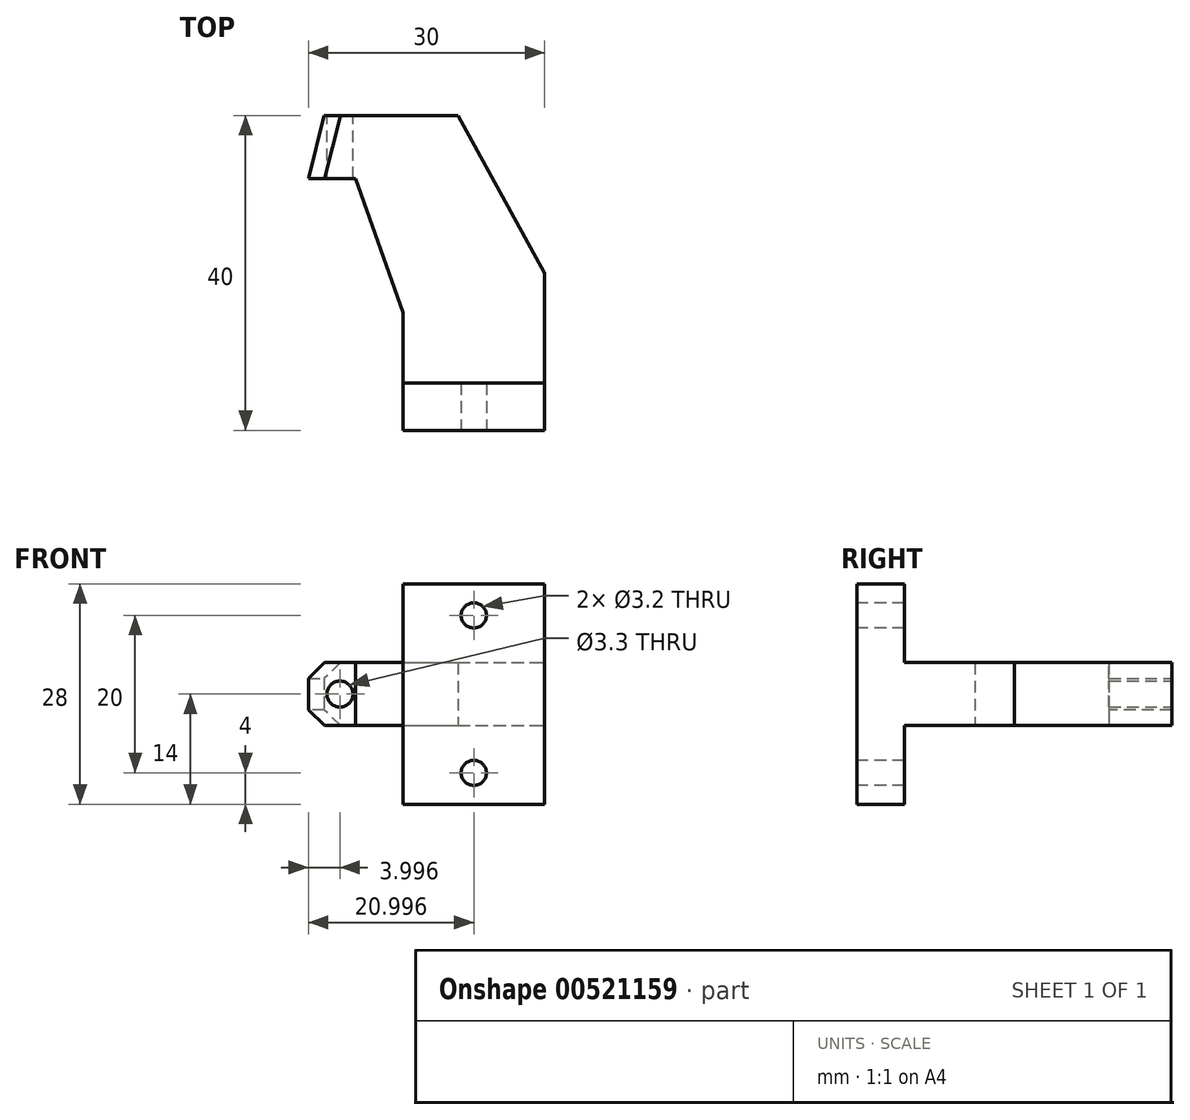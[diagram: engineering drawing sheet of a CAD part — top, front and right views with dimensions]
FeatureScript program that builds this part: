
annotation { "Feature Type Name" : "Feature", "Feature Type Description" : "" }
export const myFeature = defineFeature(function(context is Context, id is Id, definition is map)
    precondition{}
    {
        {
            var Q0;
            Q0=qCreatedBy(makeId("Top.planeOp"),FACE);
            var sketch = newSketch(context, id + "F0", { "sketchPlane" : qUnion([Q0])});
            skLineSegment(sketch, "E0", {"start": v(-19.88, 17) * mm, "end": v(-17.88, 25) * mm});
            skLineSegment(sketch, "E1", {"start": v(-17.88, 25) * mm, "end": v(-0.88, 25) * mm});
            skLineSegment(sketch, "E2", {"start": v(-0.88, 25) * mm, "end": v(10.12, 5) * mm});
            skLineSegment(sketch, "E3", {"start": v(10.12, 5) * mm, "end": v(10.12, -15) * mm});
            skLineSegment(sketch, "E4", {"start": v(-7.88, -15) * mm, "end": v(-7.88, 0) * mm});
            skLineSegment(sketch, "E5", {"start": v(-7.88, 0) * mm, "end": v(-13.88, 17) * mm});
            skLineSegment(sketch, "E6", {"start": v(-13.88, 17) * mm, "end": v(-19.88, 17) * mm});
            skLineSegment(sketch, "E7", {"start": v(-7.88, -15) * mm, "end": v(10.12, -15) * mm});
            skSolve(sketch);
        }
        {
            var Q0;
            Q0 = qSketchRegion(id + "F0", true);
            extrude(context, id + "F1", {"entities" : qUnion([Q0]), "depth" : 8 * mm, "offsetDistance" : 25 * mm});
        }
        {
            var Q0;
            Q0=makeQuery(id+"F1.opExtrude","CAP_FACE",FACE,{"disambiguationData":[OSD([sQuery(id+"F0.wireOp",EDGE,"E0"),sQuery(id+"F0.wireOp",EDGE,"E1"),sQuery(id+"F0.wireOp",EDGE,"E2"),sQuery(id+"F0.wireOp",EDGE,"E3"),sQuery(id+"F0.wireOp",EDGE,"E4"),sQuery(id+"F0.wireOp",EDGE,"E5"),sQuery(id+"F0.wireOp",EDGE,"E6"),sQuery(id+"F0.wireOp",EDGE,"E7")])],"isStart":false});
            var sketch = newSketch(context, id + "F2", { "sketchPlane" : qUnion([Q0])});
            skLineSegment(sketch, "E8.bottom", {"start": v(-7.88, -15) * mm, "end": v(10.12, -15) * mm});
            skLineSegment(sketch, "E8.top", {"start": v(-7.88, -9) * mm, "end": v(10.12, -9) * mm});
            skLineSegment(sketch, "E8.left", {"start": v(-7.88, -15) * mm, "end": v(-7.88, -9) * mm});
            skLineSegment(sketch, "E8.right", {"start": v(10.12, -15) * mm, "end": v(10.12, -9) * mm});
            skSolve(sketch);
        }
        {
            var Q0;
            Q0 = qSketchRegion(id + "F2", true);
            extrude(context, id + "F3", {"entities" : qUnion([Q0]), "operationType" : NewBodyOperationType.ADD, "depth" : 10 * mm, "offsetDistance" : 25 * mm});
        }
        {
            var Q0;
            Q0=makeQuery(id+"F1.opExtrude","CAP_FACE",FACE,{"disambiguationData":[OSD([sQuery(id+"F0.wireOp",EDGE,"E0"),sQuery(id+"F0.wireOp",EDGE,"E1"),sQuery(id+"F0.wireOp",EDGE,"E2"),sQuery(id+"F0.wireOp",EDGE,"E3"),sQuery(id+"F0.wireOp",EDGE,"E4"),sQuery(id+"F0.wireOp",EDGE,"E5"),sQuery(id+"F0.wireOp",EDGE,"E6"),sQuery(id+"F0.wireOp",EDGE,"E7")])],"isStart":true});
            var sketch = newSketch(context, id + "F4", { "sketchPlane" : qUnion([Q0])});
            skLineSegment(sketch, "E9.bottom", {"start": v(-7.88, 15) * mm, "end": v(10.12, 15) * mm});
            skLineSegment(sketch, "E9.top", {"start": v(-7.88, 9) * mm, "end": v(10.12, 9) * mm});
            skLineSegment(sketch, "E9.left", {"start": v(-7.88, 15) * mm, "end": v(-7.88, 9) * mm});
            skLineSegment(sketch, "E9.right", {"start": v(10.12, 15) * mm, "end": v(10.12, 9) * mm});
            skSolve(sketch);
        }
        {
            var Q0;
            Q0 = qSketchRegion(id + "F4", true);
            extrude(context, id + "F5", {"entities" : qUnion([Q0]), "operationType" : NewBodyOperationType.ADD, "depth" : 10 * mm, "offsetDistance" : 25 * mm});
        }
        {
            var Q0;
            Q0=makeQuery(id+"F1.opExtrude","CAP_EDGE",EDGE,{"disambiguationData":[OSD([sQuery(id+"F0.wireOp",EDGE,"E0")])],"isStart":true});
            chamfer(context, id + "F6", {"entities" : qUnion([Q0]), "width" : 2 * mm, "tangentPropagation" : true});
        }
        {
            var Q0;
            Q0=makeQuery(id+"F1.opExtrude","CAP_EDGE",EDGE,{"disambiguationData":[OSD([sQuery(id+"F0.wireOp",EDGE,"E0")])],"isStart":false});
            chamfer(context, id + "F7", {"entities" : qUnion([Q0]), "width" : 2 * mm, "tangentPropagation" : true});
        }
        {
            var Q0;
            Q0=makeQuery(id+"F1.opExtrude","SWEPT_FACE",FACE,{"disambiguationData":[OSD([sQuery(id+"F0.wireOp",EDGE,"E1")])]});
            var sketch = newSketch(context, id + "F8", { "sketchPlane" : qUnion([Q0])});
            skCircle(sketch, "E10", {"center": v(15.88, 4) * mm, "radius": 1.65 * mm});
            skSolve(sketch);
        }
        {
            var Q0;
            Q0 = qSketchRegion(id + "F8", true);
            extrude(context, id + "F9", {"entities" : qUnion([Q0]), "operationType" : NewBodyOperationType.REMOVE, "oppositeDirection" : true, "depth" : 25 * mm, "offsetDistance" : 25 * mm});
        }
        {
            var Q0;
            Q0=makeQuery(id+"F5.boolean.opBoolean","MERGE",FACE,{"derivedFrom":[makeQuery(id+"F3.boolean.opBoolean","MERGE",FACE,{"derivedFrom":[makeQuery(id+"F1.opExtrude","SWEPT_FACE",FACE,{"disambiguationData":[OSD([sQuery(id+"F0.wireOp",EDGE,"E7")])]}),makeQuery(id+"F3.opExtrude","SWEPT_FACE",FACE,{"disambiguationData":[OSD([sQuery(id+"F2.wireOp",EDGE,"E8.bottom")])]})]}),makeQuery(id+"F5.opExtrude","SWEPT_FACE",FACE,{"disambiguationData":[OSD([sQuery(id+"F4.wireOp",EDGE,"E9.bottom")])]})]});
            var sketch = newSketch(context, id + "F10", { "sketchPlane" : qUnion([Q0])});
            skCircle(sketch, "E11", {"center": v(1.12, 14) * mm, "radius": 1.6 * mm});
            skCircle(sketch, "E12.0.1.0", {"center": v(1.12, -6) * mm, "radius": 1.6 * mm});
            skLineSegment(sketch, "E12.direction1", {"start": v(1.12, 14) * mm, "end": v(25.12, 14) * mm, "construction": true});
            skLineSegment(sketch, "E12.direction2", {"start": v(1.12, 14) * mm, "end": v(1.12, -6) * mm, "construction": true});
            skSolve(sketch);
        }
        {
            var Q0;
            Q0 = qSketchRegion(id + "F10", true);
            extrude(context, id + "F11", {"entities" : qUnion([Q0]), "operationType" : NewBodyOperationType.REMOVE, "oppositeDirection" : true, "depth" : 25 * mm, "offsetDistance" : 25 * mm});
        }
    });
